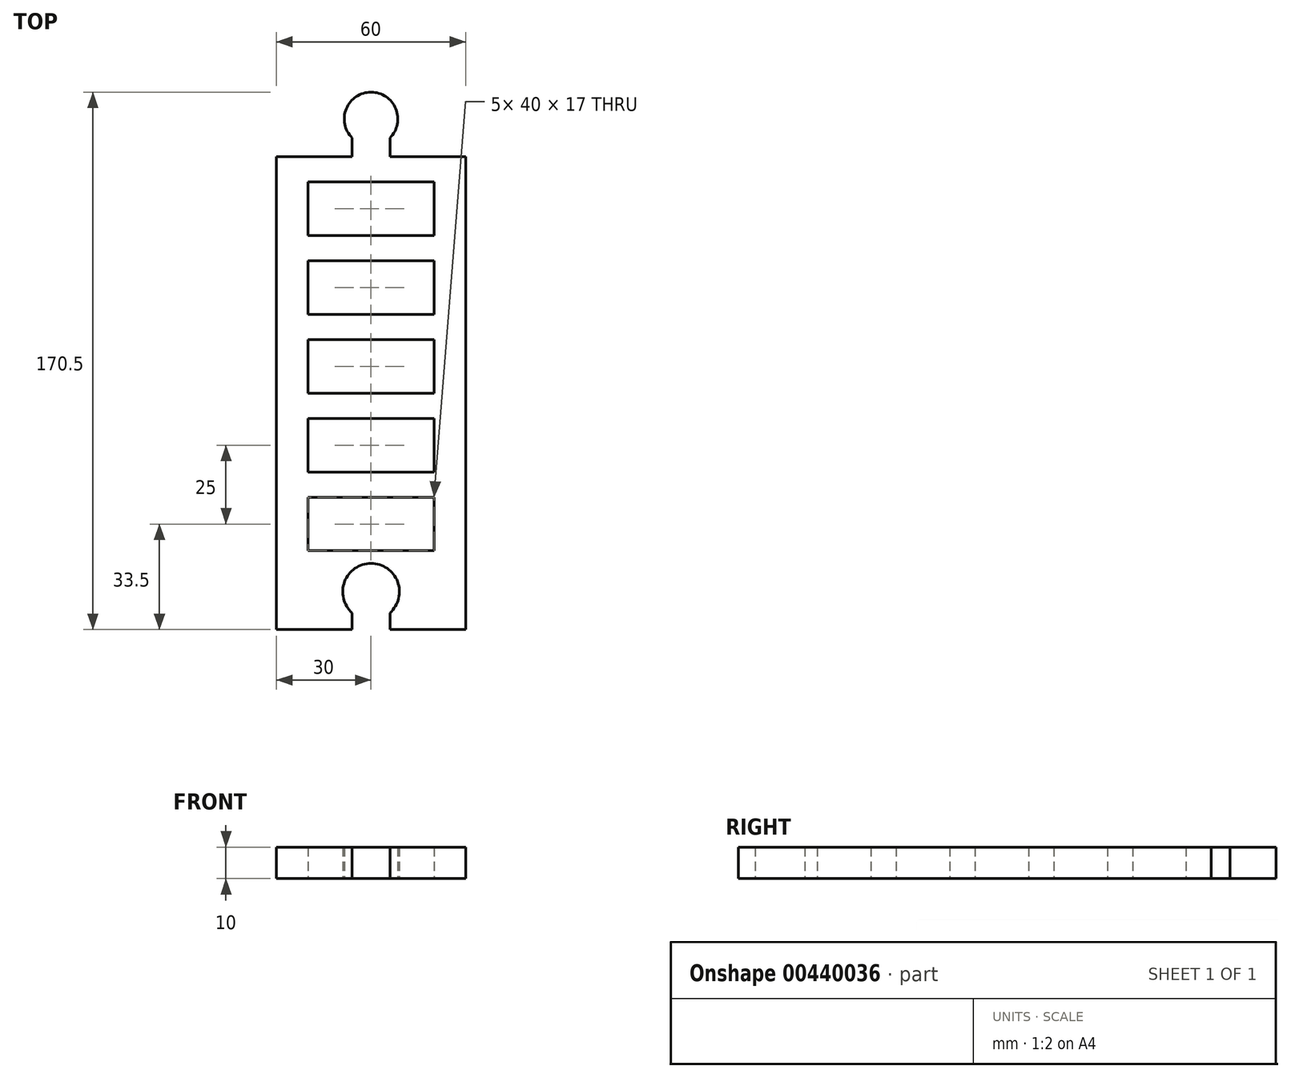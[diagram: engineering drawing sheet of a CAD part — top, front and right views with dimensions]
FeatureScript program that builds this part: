
annotation { "Feature Type Name" : "Feature", "Feature Type Description" : "" }
export const myFeature = defineFeature(function(context is Context, id is Id, definition is map)
    precondition{}
    {
        {
            var Q0;
            Q0=qCreatedBy(makeId("Top.planeOp"),FACE);
            var sketch = newSketch(context, id + "F0", { "sketchPlane" : qUnion([Q0])});
            skLineSegment(sketch, "E0.bottom", {"start": v(-30, 75) * mm, "end": v(-6, 75) * mm});
            skLineSegment(sketch, "E0.top", {"start": v(-30, -75) * mm, "end": v(-6, -75) * mm});
            skLineSegment(sketch, "E0.left", {"start": v(-30, 75) * mm, "end": v(-30, -75) * mm});
            skLineSegment(sketch, "E0.right", {"start": v(30, 75) * mm, "end": v(30, -75) * mm});
            skArc(sketch, "E1", {"start": v(6, -69.7) * mm, "mid": v(0, -54) * mm, "end": v(-6, -69.7) * mm});
            skLineSegment(sketch, "E2", {"start": v(-6, -75) * mm, "end": v(-6, -69.7) * mm});
            skLineSegment(sketch, "E3", {"start": v(6, -75) * mm, "end": v(6, -69.7) * mm});
            skArc(sketch, "E4", {"start": v(6, 80.98) * mm, "mid": v(0, 95.5) * mm, "end": v(-6, 80.98) * mm});
            skLineSegment(sketch, "E5", {"start": v(-6, 75) * mm, "end": v(-6, 80.98) * mm});
            skLineSegment(sketch, "E6", {"start": v(6, 75) * mm, "end": v(6, 80.98) * mm});
            skLineSegment(sketch, "E7.trimOffspring", {"start": v(6, -75) * mm, "end": v(30, -75) * mm});
            skLineSegment(sketch, "E8.trimOffspring", {"start": v(6, 75) * mm, "end": v(30, 75) * mm});
            skLineSegment(sketch, "E9.bottom", {"start": v(-20, 67) * mm, "end": v(20, 67) * mm});
            skLineSegment(sketch, "E9.top", {"start": v(-20, 50) * mm, "end": v(20, 50) * mm});
            skLineSegment(sketch, "E9.left", {"start": v(-20, 67) * mm, "end": v(-20, 50) * mm});
            skLineSegment(sketch, "E9.right", {"start": v(20, 67) * mm, "end": v(20, 50) * mm});
            skLineSegment(sketch, "E10.bottom", {"start": v(-20, 42) * mm, "end": v(20, 42) * mm});
            skLineSegment(sketch, "E10.top", {"start": v(-20, 25) * mm, "end": v(20, 25) * mm});
            skLineSegment(sketch, "E10.left", {"start": v(-20, 42) * mm, "end": v(-20, 25) * mm});
            skLineSegment(sketch, "E10.right", {"start": v(20, 42) * mm, "end": v(20, 25) * mm});
            skLineSegment(sketch, "E11.bottom", {"start": v(-20, 17) * mm, "end": v(20, 17) * mm});
            skLineSegment(sketch, "E11.top", {"start": v(-20, 0) * mm, "end": v(20, 0) * mm});
            skLineSegment(sketch, "E11.left", {"start": v(-20, 17) * mm, "end": v(-20, 0) * mm});
            skLineSegment(sketch, "E11.right", {"start": v(20, 17) * mm, "end": v(20, 0) * mm});
            skLineSegment(sketch, "E12.bottom", {"start": v(-20, -8) * mm, "end": v(20, -8) * mm});
            skLineSegment(sketch, "E12.top", {"start": v(-20, -25) * mm, "end": v(20, -25) * mm});
            skLineSegment(sketch, "E12.left", {"start": v(-20, -8) * mm, "end": v(-20, -25) * mm});
            skLineSegment(sketch, "E12.right", {"start": v(20, -8) * mm, "end": v(20, -25) * mm});
            skLineSegment(sketch, "E13.bottom", {"start": v(-20, -33) * mm, "end": v(20, -33) * mm});
            skLineSegment(sketch, "E13.top", {"start": v(-20, -50) * mm, "end": v(20, -50) * mm});
            skLineSegment(sketch, "E13.left", {"start": v(-20, -33) * mm, "end": v(-20, -50) * mm});
            skLineSegment(sketch, "E13.right", {"start": v(20, -33) * mm, "end": v(20, -50) * mm});
            skSolve(sketch);
        }
        {
            var Q0;
            Q0 = qSketchRegion(id + "F0", true);
            extrude(context, id + "F1", {"entities" : qUnion([Q0]), "depth" : 10 * mm});
        }
    });
